# Revit family: Małe wentylatory promieniowe FRv 075-110+
name_source: partatom
category: Mechanical Equipment
revit_build: Autodesk Revit 2015 (Build: 20140606_1530(x64)
units: mm (PartAtom-declared; Revit-internal decimal feet)

## types (1)
- Małe wentylatory promieniowe FRv 075-110+
    Ciśnienie maksymalne = 54,00 Pa
    Manufacturer = Chemowent
    Moc nominalna = 0 kW
    Natężenie znamionowe = 0 A
    Prędkość obrotowa = 1500
    URL = http://chemowent.pl
    Waga = 5,00 kg
    Wydajność maksymalna = 115,00 m³/h
    dia / 2 = 38 mm
    dia silnika = 43 mm
    ex. face = 124 mm  [stored 0.406824 ft]
    kołnierz = Yes
    kołnierz - mimośród = 13 mm
    kołnierz - umiejscowienie = 68 mm  [stored 0.223097 ft]
    kołnierz - średnica = 99 mm  [stored 0.324803 ft]
    mimośród silnika = 0 mm  [stored 0 ft]
    odl. czoła od osi = 98 mm  [stored 0.321522 ft]
    odlęgłość osiowa = 86 mm  [stored 0.282152 ft]
    podstawa = No
    podstawa - głębokość = 110 mm  [stored 0.360892 ft]
    podstawa - umiejscowienie = 66 mm  [stored 0.216535 ft]
    szerokość podstawy = 186 mm  [stored 0.610236 ft]
    wysokość 1 = 150 mm
    wysokość 2 = 160 mm  [stored 0.524934 ft]
    łączna głębokość = 255 mm  [stored 0.836614 ft]
    średnica nominalna = 75 mm
    średnica wentylatora = 112 mm

note: [stored X ft] marks values corroborated as IEEE doubles in the binary element streams (Revit-internal decimal feet)

## geometry (parser evidence)
native form markers: Sweep x3
no freeform markers — native parametric forms only
